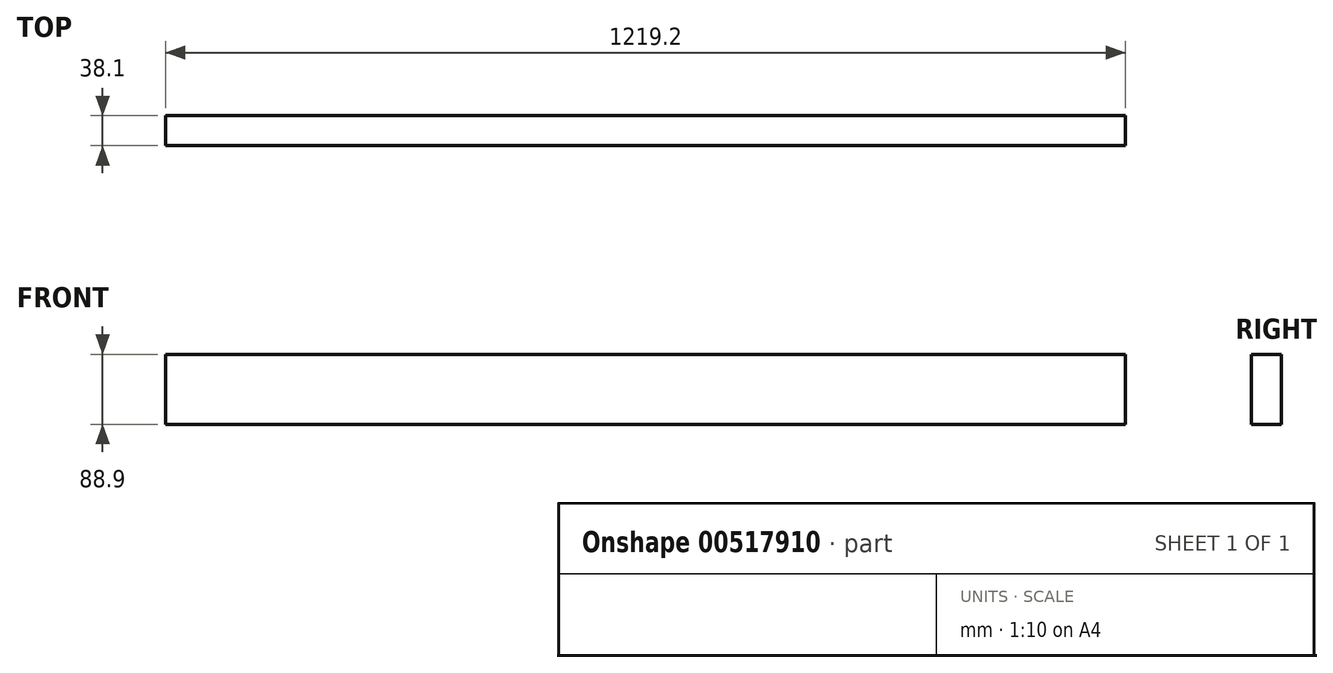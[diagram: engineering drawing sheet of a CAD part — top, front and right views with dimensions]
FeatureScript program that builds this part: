
annotation { "Feature Type Name" : "Feature", "Feature Type Description" : "" }
export const myFeature = defineFeature(function(context is Context, id is Id, definition is map)
    precondition{}
    {
        {
            var Q0;
            Q0=qCreatedBy(makeId("Right.planeOp"),FACE);
            var sketch = newSketch(context, id + "F0", { "sketchPlane" : qUnion([Q0])});
            skLineSegment(sketch, "E0.bottom", {"start": v(19.05, 44.45) * mm, "end": v(-19.05, 44.45) * mm});
            skLineSegment(sketch, "E0.top", {"start": v(19.05, -44.45) * mm, "end": v(-19.05, -44.45) * mm});
            skLineSegment(sketch, "E0.left", {"start": v(19.05, 44.45) * mm, "end": v(19.05, -44.45) * mm});
            skLineSegment(sketch, "E0.right", {"start": v(-19.05, 44.45) * mm, "end": v(-19.05, -44.45) * mm});
            skPoint(sketch, "E0.middle", {"position": v(0, 0) * mm});
            skSolve(sketch);
        }
        {
            var Q0;
            Q0=makeQuery(id+"F0.imprint","IMPRINT",FACE,{"disambiguationData":[TD([[makeQuery(id+"F0.imprint","IMPRINT",EDGE,{"derivedFrom":sQuery(id+"F0.wireOp",EDGE,"E0.bottom")}),1.0]])]});
            extrude(context, id + "F1", {"entities" : qUnion([Q0]), "endBound" : BoundingType.SYMMETRIC, "depth" : 1219.2 * mm, "offsetDistance" : 25.4 * mm});
        }
    });
